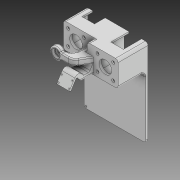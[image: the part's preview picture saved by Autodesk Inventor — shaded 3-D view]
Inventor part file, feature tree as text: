
AUTODESK INVENTOR PART (.ipt)
format: ipt  version: 2020 (Build 240168000, 168)  size: 778,752 bytes
history: native  units: mm
features: sketch x22, extrude x21, projected_geometry x5, plane x4, fillet x3, revolve x2, chamfer x1
ambient origin geometry x8: Origin, YZ Plane, XZ Plane, XY Plane, X Axis, Y Axis, Z Axis, Center Point
bodies: Solid1 (feature_tree)
feature tree (58):
  extrude  "Extrusion1"  Depth=120.0mm
  extrude  "Extrusion2"  Depth=55.0mm TaperAngle=0.0deg
  extrude  "Extrusion3"  Depth=44.0mm
  extrude  "Extrusion4"  Depth=25.0mm
  extrude  "Extrusion5"  Depth=25.0mm TaperAngle=0.0deg
  extrude  "Extrusion6"  Depth=3.5mm
  extrude  "Extrusion7"  TaperAngle=0.0deg  [1 undecoded]
  extrude  "Extrusion8"  Depth=21.0mm TaperAngle=0.0deg
  extrude  "Extrusion9"  Depth=14.0mm TaperAngle=0.0deg
  extrude  "Extrusion10"  Depth=2.5mm TaperAngle=0.0deg
  extrude  "Extrusion11"  Depth=2.5mm TaperAngle=0.0deg
  extrude  "Extrusion13"  Depth=44.0mm
  extrude  "Extrusion15"  Depth=3.0mm
  extrude  "Extrusion16"  Depth=3.0mm
  extrude  "Extrusion17"  Depth=28.0mm
  chamfer  "Chamfer2"  Distance=25.0mm
  plane  "Work Plane1"
  extrude  "Extrusion18"  Depth=25.0mm TaperAngle=0.0deg
  extrude  "Extrusion19"  Depth=12.5mm
  plane  "Work Plane2"
  sketch  "Sketch25"  dims[d69=72.0mm d70=3.621558mm d71=3.621558mm d72=5.0mm d73=3.5mm]
  revolve  "Revolution1"  [1 undecoded]
  revolve  "Revolution2"  [1 undecoded]
  fillet  "Fillet3"  Radius=3.621558mm
  fillet  "Fillet4"  Radius=5.0mm
  fillet  "Fillet5"  Radius=3.5mm
  extrude  "Extrusion22"  Depth=9.0mm
  extrude  "Extrusion23"  Depth=4.0mm
  plane  "Work Plane3"
  plane  "Work Plane4"
  extrude  "Extrusion24"  Depth=8.0mm
  extrude  "Extrusion25"  Depth=8.0mm
  sketch  "Sketch1"  dims[d1=122.0mm d3=120.0mm]
  sketch  "Sketch2"  dims[d4=4.0mm d5=0.0mm d6=55.0mm d7=0.0mm]
  sketch  "Sketch3"  dims[d8=44.0mm d9=44.0mm]
  sketch  "Sketch4"  dims[d10=44.0mm d11=25.0mm]
  sketch  "Sketch5"  dims[d12=25.0mm d14=20.0mm d15=0.0mm]
  sketch  "Sketch6"  dims[d16=31.0mm d17=3.5mm]
  sketch  "Sketch7"  dims[d18=25.0mm d19=0.0mm d20=0.0mm]
  projected_geometry  "Projected Loop1"
  sketch  "Sketch8"  dims[d21=25.0mm d22=21.0mm d23=0.0mm]
  sketch  "Sketch9"  dims[d24=14.0mm d25=0.0mm d26=14.0mm d27=0.0mm]
  sketch  "Sketch10"  dims[d28=6.0mm d29=2.5mm d30=0.0mm]
  sketch  "Sketch11"  dims[d31=6.0mm d32=2.5mm d33=0.0mm]
  sketch  "Sketch13"  dims[d35=44.0mm d36=44.0mm]
  sketch  "Sketch15"  dims[d37=3.0mm d38=3.0mm]
  sketch  "Sketch17"  dims[d39=25.0mm d40=3.0mm]
  projected_geometry  "Projected Loop2"
  sketch  "Sketch18"  dims[d41=3.0mm d42=28.0mm]
  sketch  "Sketch19"  dims[d44=22.0mm d45=25.0mm d46=0.0mm]
  sketch  "Sketch20"  dims[d47=21.0mm d51=25.0mm d52=0.0mm]
  sketch  "Sketch23"  dims[d53=12.5mm d59=2.4mm d60=12.5mm d61=20.5mm]
  sketch  "Sketch24"  dims[d64=90.974mm d65=0.0mm d68=72.0mm]
  projected_geometry  "Projected Loop3"
  sketch  "Sketch26"  dims[d77=2.0mm d78=9.0mm]
  projected_geometry  "Projected Loop4"
  sketch  "Sketch27"  dims[d79=22.68928mm d80=20.0mm d81=8.0mm d82=8.0mm d83=8.0mm d84=32.0mm d85=9.0mm d86=1.5mm d87=0.0mm d93=15.0mm d94=0.0mm d95=8.0mm d96=2.0mm d97=3.0mm d98=0.0mm d99=0.5mm d100=2.0mm d101=45.0deg d103=31.0mm d105=9.0mm d106=150.0deg d107=15.0deg d108=5.0mm d109=12.0mm d110=0.0mm d111=5.3mm d112=0.0mm d113=0.0mm d117=3.0mm d121=15.0mm d122=7.0mm d123=12.0mm d125=5.0mm d126=2.0mm d127=8.0mm d128=141.0mm d129=21.0mm d130=15.0mm d131=15.0mm d132=15.0mm d133=15.0mm d134=10.0mm d135=12.0mm d136=2.5mm d137=0.0mm d138=10.0mm d139=0.0mm d141=8.125mm d142=3.5mm d143=90.0deg d144=90.0deg d145=2.0mm d146=0.5mm d147=5.0mm d148=4.0mm d149=0.5mm d150=-5.0mm d151=-5.0mm d152=20.0mm d153=0.0mm d154=20.0mm d155=0.0mm]
  projected_geometry  "Projected Loop5"
note: 3 required parameter values undecoded (feature->parameter linkage not recoverable at this tier; creation-order binding heuristic only, values carry confidence <= 0.55)